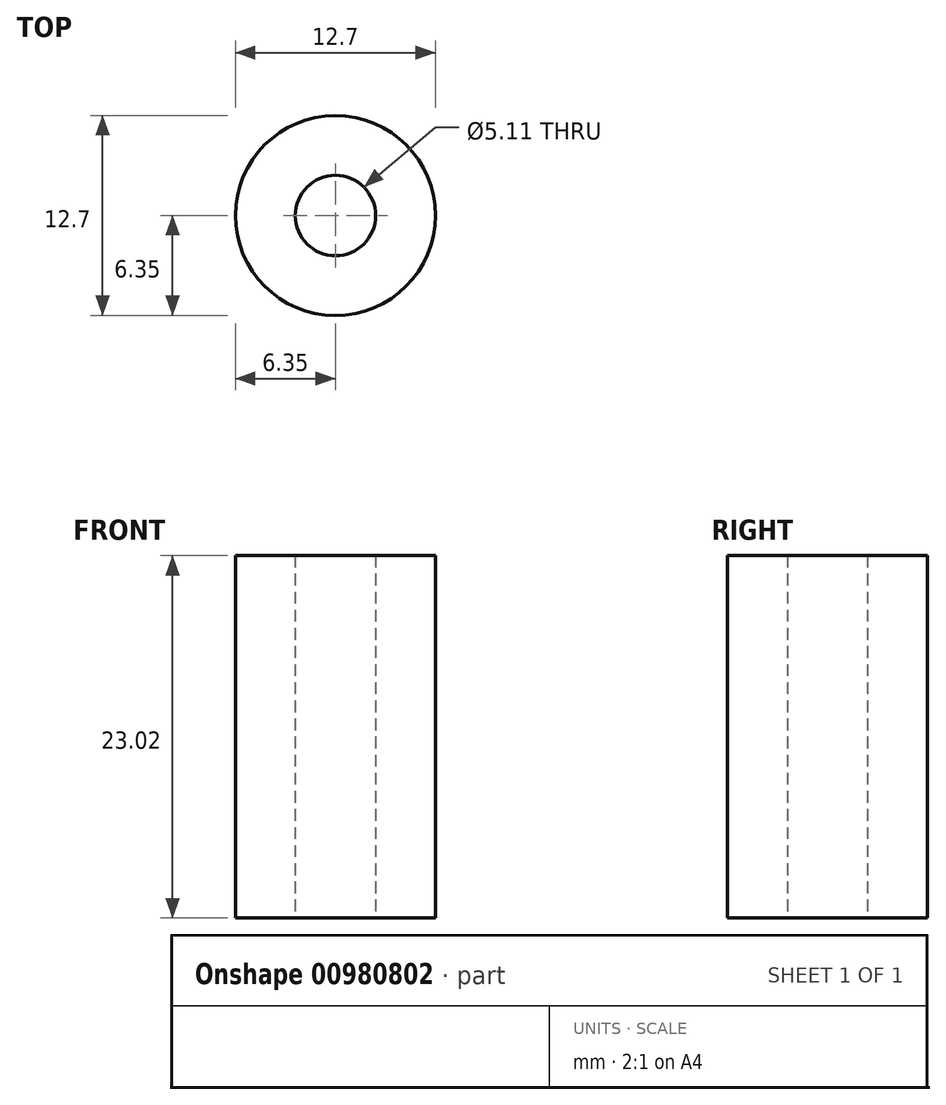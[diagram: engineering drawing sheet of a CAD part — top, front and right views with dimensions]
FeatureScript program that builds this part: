
annotation { "Feature Type Name" : "Feature", "Feature Type Description" : "" }
export const myFeature = defineFeature(function(context is Context, id is Id, definition is map)
    precondition{}
    {
        {
            var Q0;
            Q0=qCreatedBy(makeId("Top.planeOp"),FACE);
            var sketch = newSketch(context, id + "F0", { "sketchPlane" : qUnion([Q0])});
            skCircle(sketch, "E0", {"center": v(0, 0) * mm, "radius": 2.55 * mm});
            skCircle(sketch, "E1", {"center": v(0, 0) * mm, "radius": 6.35 * mm});
            skSolve(sketch);
        }
        {
            var Q0;
            Q0=qSketchRegion(id+"F0",true);
            extrude(context, id + "F1", {"entities" : qUnion([Q0]), "depth" : 23.02 * mm, "offsetDistance" : 25.4 * mm});
        }
    });
